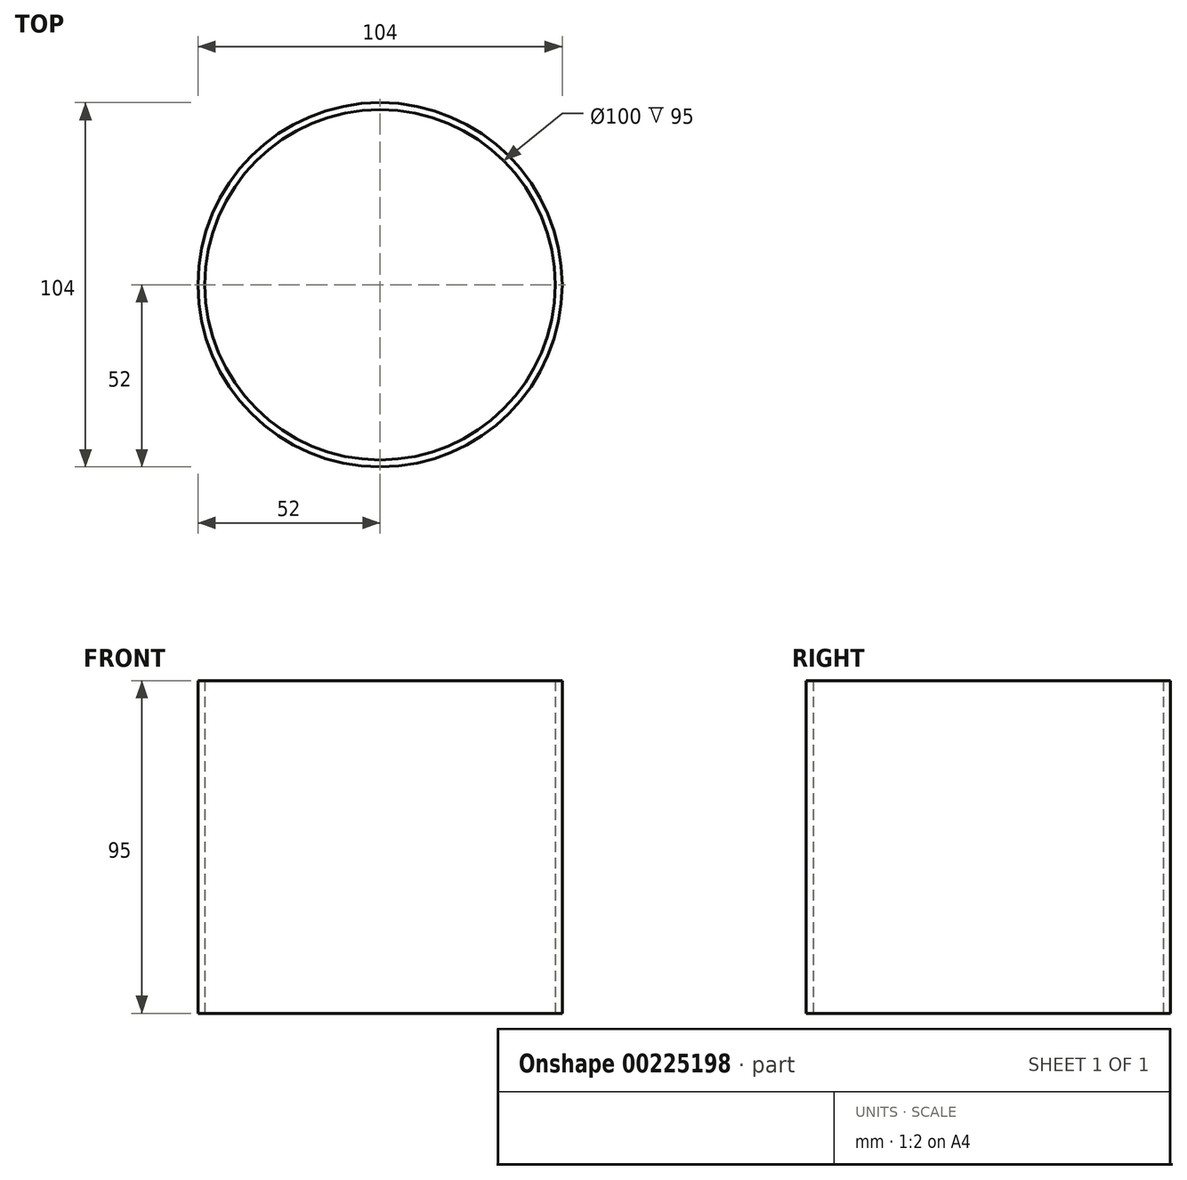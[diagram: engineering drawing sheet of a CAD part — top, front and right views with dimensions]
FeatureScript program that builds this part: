
annotation { "Feature Type Name" : "Feature", "Feature Type Description" : "" }
export const myFeature = defineFeature(function(context is Context, id is Id, definition is map)
    precondition{}
    {
        {
            var Q0;
            Q0=qCreatedBy(makeId("Top.planeOp"),FACE);
            var sketch = newSketch(context, id + "F0", { "sketchPlane" : qUnion([Q0])});
            skCircle(sketch, "E0", {"center": v(0, 0) * mm, "radius": 50 * mm});
            skCircle(sketch, "E1", {"center": v(0, 0) * mm, "radius": 52 * mm});
            skSolve(sketch);
        }
        {
            var Q0;
            Q0=makeQuery(id+"F0.imprint","IMPRINT",FACE,{"disambiguationData":[TD([[makeQuery(id+"F0.imprint","IMPRINT",EDGE,{"derivedFrom":sQuery(id+"F0.wireOp",EDGE,"E0")}),-1.0]])]});
            extrude(context, id + "F1", {"entities" : qUnion([Q0]), "depth" : 95 * mm});
        }
    });
